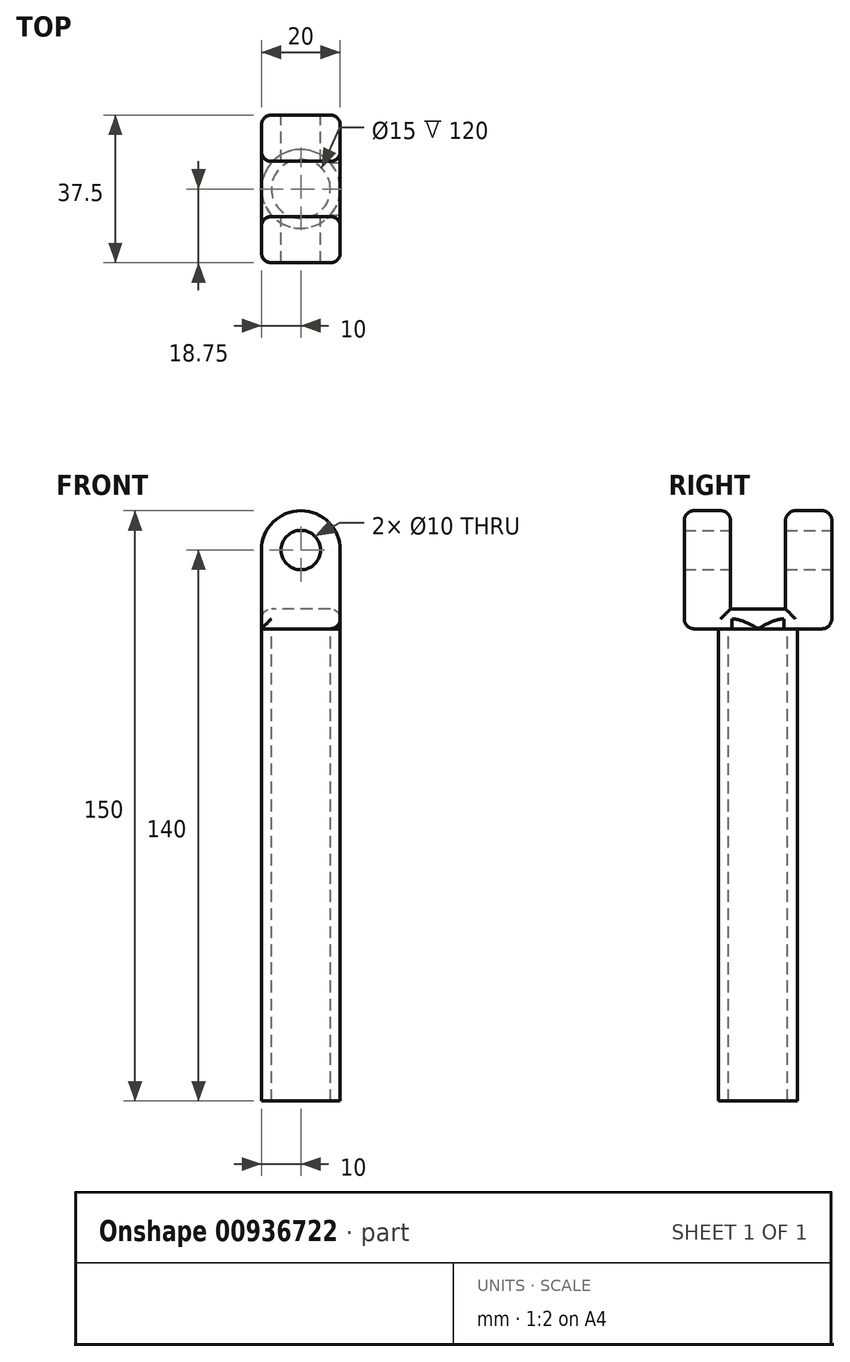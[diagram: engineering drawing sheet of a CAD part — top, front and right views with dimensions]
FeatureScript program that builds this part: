
annotation { "Feature Type Name" : "Feature", "Feature Type Description" : "" }
export const myFeature = defineFeature(function(context is Context, id is Id, definition is map)
    precondition{}
    {
        {
            var Q0;
            Q0=qCreatedBy(makeId("Front.planeOp"),FACE);
            var sketch = newSketch(context, id + "F0", { "sketchPlane" : qUnion([Q0])});
            skCircle(sketch, "E0", {"center": v(0, 20) * mm, "radius": 5 * mm});
            skArc(sketch, "E1", {"start": v(10, 20) * mm, "mid": v(0, 30) * mm, "end": v(-10, 20) * mm});
            skLineSegment(sketch, "E2", {"start": v(10, 20) * mm, "end": v(10, 0) * mm});
            skLineSegment(sketch, "E3", {"start": v(-10, 20) * mm, "end": v(-10, 0) * mm});
            skLineSegment(sketch, "E4", {"start": v(-10, 0) * mm, "end": v(10, 0) * mm});
            skSolve(sketch);
        }
        {
            var Q0;
            Q0=makeQuery(id+"F0.imprint","IMPRINT",FACE,{"disambiguationData":[TD([[makeQuery(id+"F0.imprint","IMPRINT",EDGE,{"derivedFrom":sQuery(id+"F0.wireOp",EDGE,"E0")}),-1.0]])]});
            extrude(context, id + "F1", {"entities" : qUnion([Q0]), "depth" : 18.75 * mm, "offsetDistance" : 25 * mm, "hasSecondDirection" : true, "secondDirectionOppositeDirection" : true, "secondDirectionDepth" : 18.75 * mm});
        }
        {
            var Q0;
            Q0=makeQuery(id+"F1.opExtrude","CAP_FACE",FACE,{"disambiguationData":[OSD([sQuery(id+"F0.wireOp",EDGE,"E0"),sQuery(id+"F0.wireOp",EDGE,"E1"),sQuery(id+"F0.wireOp",EDGE,"E2"),sQuery(id+"F0.wireOp",EDGE,"E3"),sQuery(id+"F0.wireOp",EDGE,"E4")])],"isStart":false});
            cPlane(context, id + "F2", {"entities" : qUnion([Q0]), "cplaneType" : CPlaneType.OFFSET, "offset" : 18.75 * mm, "oppositeDirection" : true, "width" : 150 * mm, "height" : 150 * mm});
        }
        {
            var Q0;
            Q0=qCreatedBy(id+"F2.planeOp",FACE);
            var sketch = newSketch(context, id + "F3", { "sketchPlane" : qUnion([Q0])});
            skLineSegment(sketch, "E5", {"start": v(0, 5) * mm, "end": v(12, 5) * mm});
            skLineSegment(sketch, "E6", {"start": v(12, 5) * mm, "end": v(12, 35) * mm});
            skLineSegment(sketch, "E7", {"start": v(12, 35) * mm, "end": v(-12, 35) * mm});
            skLineSegment(sketch, "E8", {"start": v(0, 5) * mm, "end": v(-12, 5) * mm});
            skLineSegment(sketch, "E9", {"start": v(-12, 5) * mm, "end": v(-12, 35) * mm});
            skSolve(sketch);
        }
        {
            var Q0;
            Q0=makeQuery(id+"F3.imprint","IMPRINT",FACE,{"disambiguationData":[TD([[makeQuery(id+"F3.imprint","IMPRINT",EDGE,{"derivedFrom":sQuery(id+"F3.wireOp",EDGE,"E5")}),1.0]])]});
            extrude(context, id + "F4", {"entities" : qUnion([Q0]), "operationType" : NewBodyOperationType.REMOVE, "oppositeDirection" : true, "depth" : 7 * mm, "offsetDistance" : 25 * mm, "hasSecondDirection" : true, "secondDirectionOppositeDirection" : false, "secondDirectionDepth" : 7 * mm});
        }
        {
            var Q0;
            Q0=makeQuery(id+"F1.opExtrude","SWEPT_FACE",FACE,{"disambiguationData":[OSD([sQuery(id+"F0.wireOp",EDGE,"E4")])]});
            cPlane(context, id + "F5", {"entities" : qUnion([Q0]), "cplaneType" : CPlaneType.OFFSET, "offset" : 0 * mm, "width" : 150 * mm, "height" : 150 * mm});
        }
        {
            var Q0;
            Q0=qCreatedBy(id+"F5.planeOp",FACE);
            var sketch = newSketch(context, id + "F6", { "sketchPlane" : qUnion([Q0])});
            skCircle(sketch, "E10", {"center": v(0, 0) * mm, "radius": 10 * mm});
            skCircle(sketch, "E11", {"center": v(0, 0) * mm, "radius": 7.5 * mm});
            skSolve(sketch);
        }
        {
            var Q0;
            Q0=makeQuery(id+"F6.imprint","IMPRINT",FACE,{"disambiguationData":[TD([[makeQuery(id+"F6.imprint","IMPRINT",EDGE,{"derivedFrom":sQuery(id+"F6.wireOp",EDGE,"E10")}),1.0]])]});
            extrude(context, id + "F7", {"entities" : qUnion([Q0]), "operationType" : NewBodyOperationType.ADD, "depth" : 120 * mm, "offsetDistance" : 25 * mm});
        }
        {
            var Q0;
            Q0=makeQuery(id+"F4.boolean.opBoolean","INTERSECT",EDGE,{"derivedFrom":[makeQuery(id+"F1.opExtrude","SWEPT_FACE",FACE,{"disambiguationData":[OSD([sQuery(id+"F0.wireOp",EDGE,"E2")])]}),makeQuery(id+"F4.opExtrude","CAP_FACE",FACE,{"disambiguationData":[OSD([sQuery(id+"F3.wireOp",EDGE,"E5"),sQuery(id+"F3.wireOp",EDGE,"E6"),sQuery(id+"F3.wireOp",EDGE,"E7"),sQuery(id+"F3.wireOp",EDGE,"E8"),sQuery(id+"F3.wireOp",EDGE,"E9")])],"isStart":true})]});
            var Q1;
            Q1=makeQuery(id+"F4.boolean.opBoolean","INTERSECT",EDGE,{"derivedFrom":[makeQuery(id+"F1.opExtrude","SWEPT_FACE",FACE,{"disambiguationData":[OSD([sQuery(id+"F0.wireOp",EDGE,"E2")])]}),makeQuery(id+"F4.opExtrude","CAP_FACE",FACE,{"disambiguationData":[OSD([sQuery(id+"F3.wireOp",EDGE,"E5"),sQuery(id+"F3.wireOp",EDGE,"E6"),sQuery(id+"F3.wireOp",EDGE,"E7"),sQuery(id+"F3.wireOp",EDGE,"E8"),sQuery(id+"F3.wireOp",EDGE,"E9")])],"isStart":false})]});
            var Q2;
            Q2=makeQuery(id+"F1.opExtrude","CAP_EDGE",EDGE,{"disambiguationData":[OSD([sQuery(id+"F0.wireOp",EDGE,"E2")])],"isStart":true});
            var Q3;
            Q3=makeQuery(id+"F1.opExtrude","CAP_EDGE",EDGE,{"disambiguationData":[OSD([sQuery(id+"F0.wireOp",EDGE,"E2")])],"isStart":false});
            var Q4;
            Q4=makeQuery(id+"F4.boolean.opBoolean","INTERSECT",EDGE,{"derivedFrom":[makeQuery(id+"F1.opExtrude","SWEPT_FACE",FACE,{"disambiguationData":[OSD([sQuery(id+"F0.wireOp",EDGE,"E2")])]}),makeQuery(id+"F4.opExtrude","SWEPT_FACE",FACE,{"disambiguationData":[OSD([sQuery(id+"F3.wireOp",EDGE,"E5"),sQuery(id+"F3.wireOp",EDGE,"E8")])]})]});
            var Q5;
            Q5=makeQuery(id+"F4.boolean.opBoolean","INTERSECT",EDGE,{"derivedFrom":[makeQuery(id+"F1.opExtrude","SWEPT_FACE",FACE,{"disambiguationData":[OSD([sQuery(id+"F0.wireOp",EDGE,"E3")])]}),makeQuery(id+"F4.opExtrude","SWEPT_FACE",FACE,{"disambiguationData":[OSD([sQuery(id+"F3.wireOp",EDGE,"E5"),sQuery(id+"F3.wireOp",EDGE,"E8")])]})]});
            var Q6;
            {var subQ0=sQuery(id+"F0.wireOp",EDGE,"E4");var subQ1=sQuery(id+"F0.wireOp",EDGE,"E2");Q6=makeQuery(id+"F7.boolean.opBoolean","SPLIT",EDGE,{"disambiguationData":[TD([makeQuery(id+"F1.opExtrude","CAP_FACE",FACE,{"disambiguationData":[OSD([sQuery(id+"F0.wireOp",EDGE,"E0"),sQuery(id+"F0.wireOp",EDGE,"E1"),subQ1,sQuery(id+"F0.wireOp",EDGE,"E3"),subQ0])],"isStart":true})])],"derivedFrom":makeQuery(id+"F1.opExtrude","SWEPT_EDGE",EDGE,{"disambiguationData":[OSD([subQ1,subQ0])]})});}
            var Q7;
            Q7=makeQuery(id+"F1.opExtrude","CAP_EDGE",EDGE,{"disambiguationData":[OSD([sQuery(id+"F0.wireOp",EDGE,"E4")])],"isStart":true});
            var Q8;
            Q8=makeQuery(id+"F1.opExtrude","CAP_EDGE",EDGE,{"disambiguationData":[OSD([sQuery(id+"F0.wireOp",EDGE,"E4")])],"isStart":false});
            fillet(context, id + "F8", {"entities" : qUnion([Q0, Q1, Q2, Q3, Q4, Q5, Q6, Q7, Q8]), "radius" : 2.5 * mm, "tangentPropagation" : true, "allowEdgeOverflow" : false});
        }
    });
